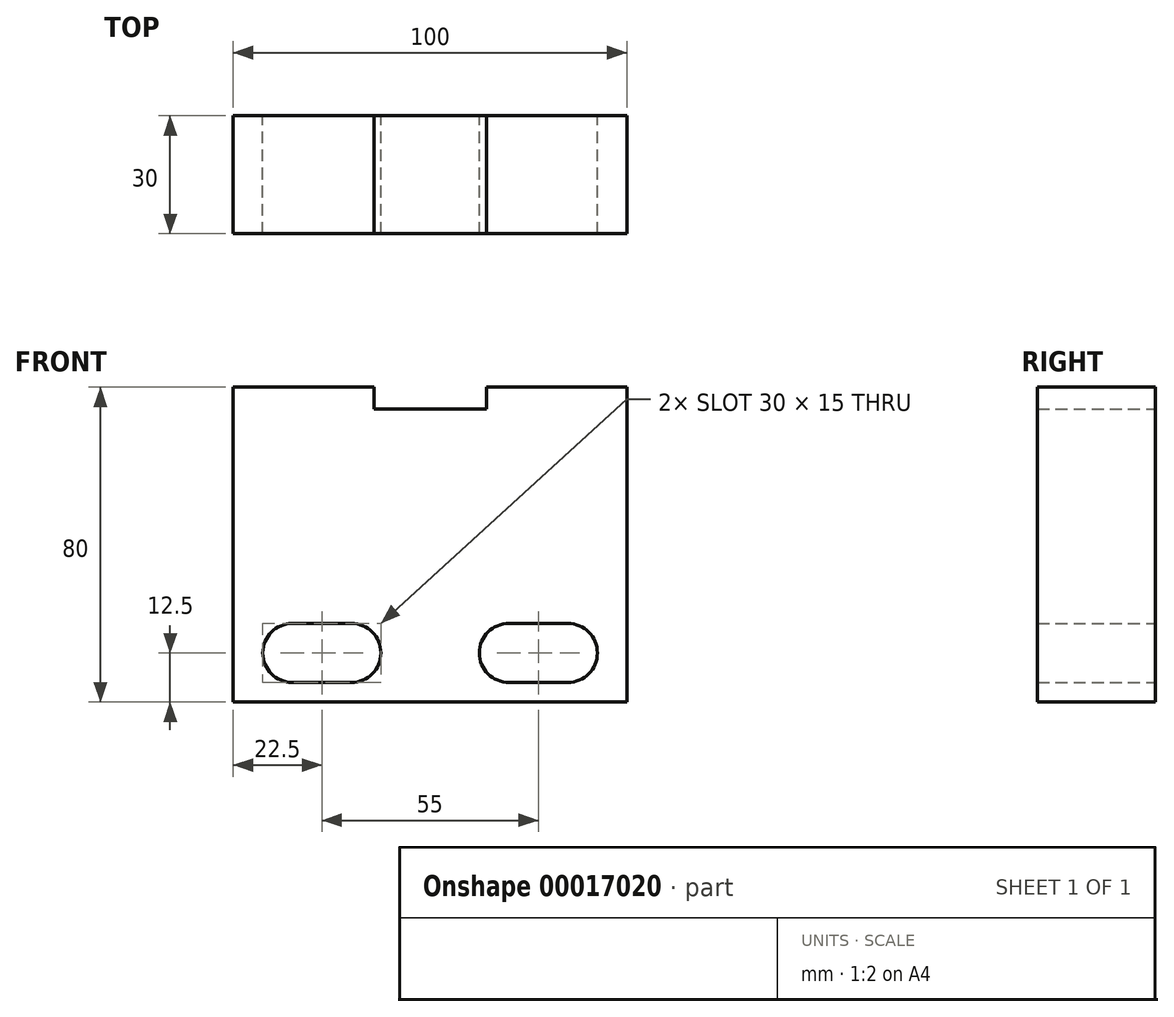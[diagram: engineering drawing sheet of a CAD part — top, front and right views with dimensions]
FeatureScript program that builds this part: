
annotation { "Feature Type Name" : "Feature", "Feature Type Description" : "" }
export const myFeature = defineFeature(function(context is Context, id is Id, definition is map)
    precondition{}
    {
        {
            var Q0;
            Q0=qCreatedBy(makeId("Front.planeOp"),FACE);
            var sketch = newSketch(context, id + "F0", { "sketchPlane" : qUnion([Q0])});
            skLineSegment(sketch, "E0.rect.bottom", {"start": v(50, -51.75) * mm, "end": v(-50, -51.75) * mm, "construction": true});
            skLineSegment(sketch, "E0.rect.top", {"start": v(50, 51.75) * mm, "end": v(-50, 51.75) * mm, "construction": true});
            skLineSegment(sketch, "E0.rect.left", {"start": v(50, -51.75) * mm, "end": v(50, 51.75) * mm, "construction": true});
            skLineSegment(sketch, "E0.rect.right", {"start": v(-50, -51.75) * mm, "end": v(-50, 51.75) * mm, "construction": true});
            skPoint(sketch, "E0.rect.middle", {"position": v(0, 0) * mm});
            skCircle(sketch, "E1", {"center": v(0, 51.75) * mm, "radius": 27.5 * mm, "construction": true});
            skLineSegment(sketch, "E2.bottom", {"start": v(-50, -51.75) * mm, "end": v(50, -51.75) * mm});
            skLineSegment(sketch, "E2.top", {"start": v(-50, 28.25) * mm, "end": v(-14.28, 28.25) * mm});
            skLineSegment(sketch, "E2.left", {"start": v(-50, -51.75) * mm, "end": v(-50, 28.25) * mm});
            skLineSegment(sketch, "E2.right", {"start": v(50, -51.75) * mm, "end": v(50, 28.25) * mm});
            skPoint(sketch, "E3", {"position": v(14.28, 28.25) * mm});
            skPoint(sketch, "E4", {"position": v(-14.28, 28.25) * mm});
            skLineSegment(sketch, "E5.top", {"start": v(14.28, 22.75) * mm, "end": v(-14.28, 22.75) * mm});
            skLineSegment(sketch, "E5.left", {"start": v(14.28, 28.25) * mm, "end": v(14.28, 22.75) * mm});
            skLineSegment(sketch, "E5.right", {"start": v(-14.28, 28.25) * mm, "end": v(-14.28, 22.75) * mm});
            skLineSegment(sketch, "E6.trimOffspring", {"start": v(14.28, 28.25) * mm, "end": v(50, 28.25) * mm});
            skLineSegment(sketch, "E7.bottom", {"start": v(35, -31.75) * mm, "end": v(20, -31.75) * mm});
            skLineSegment(sketch, "E7.top", {"start": v(35, -46.75) * mm, "end": v(20, -46.75) * mm});
            skArc(sketch, "E8", {"start": v(35, -46.75) * mm, "mid": v(42.5, -39.25) * mm, "end": v(35, -31.75) * mm});
            skArc(sketch, "E9", {"start": v(20, -31.75) * mm, "mid": v(12.5, -39.25) * mm, "end": v(20, -46.75) * mm});
            skLineSegment(sketch, "E10.bottom", {"start": v(-20, -31.75) * mm, "end": v(-35, -31.75) * mm});
            skArc(sketch, "E11", {"start": v(-20, -46.75) * mm, "mid": v(-12.5, -39.25) * mm, "end": v(-20, -31.75) * mm});
            skArc(sketch, "E12", {"start": v(-35, -31.75) * mm, "mid": v(-42.5, -39.25) * mm, "end": v(-35, -46.75) * mm});
            skLineSegment(sketch, "E10.top", {"start": v(-20, -46.75) * mm, "end": v(-35, -46.75) * mm});
            skSolve(sketch);
        }
        {
            var Q0;
            Q0 = qSketchRegion(id + "F0", true);
            extrude(context, id + "F1", {"entities" : qUnion([Q0]), "depth" : 30 * mm});
        }
    });
